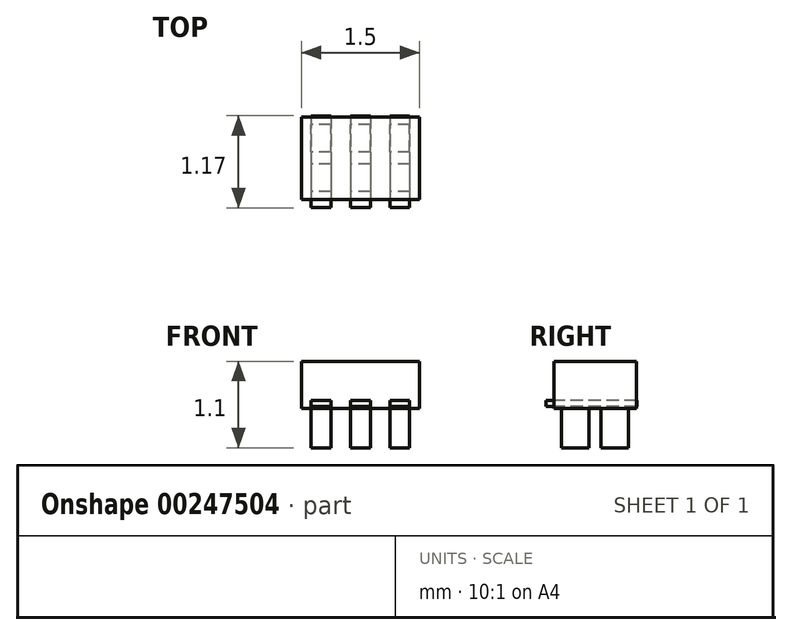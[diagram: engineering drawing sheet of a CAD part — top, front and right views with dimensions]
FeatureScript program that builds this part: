
annotation { "Feature Type Name" : "Feature", "Feature Type Description" : "" }
export const myFeature = defineFeature(function(context is Context, id is Id, definition is map)
    precondition{}
    {
        {
            var Q0;
            Q0=qCreatedBy(makeId("Top.planeOp"),FACE);
            var sketch = newSketch(context, id + "F0", { "sketchPlane" : qUnion([Q0])});
            skLineSegment(sketch, "E0.bottom", {"start": v(0.75, -0.53) * mm, "end": v(-0.75, -0.53) * mm});
            skLineSegment(sketch, "E0.top", {"start": v(0.75, 0.53) * mm, "end": v(-0.75, 0.53) * mm});
            skLineSegment(sketch, "E0.left", {"start": v(0.75, -0.53) * mm, "end": v(0.75, 0.53) * mm});
            skLineSegment(sketch, "E0.right", {"start": v(-0.75, -0.53) * mm, "end": v(-0.75, 0.52) * mm});
            skPoint(sketch, "E0.middle", {"position": v(0, 0) * mm});
            skSolve(sketch);
        }
        {
            var Q0;
            Q0=qSketchRegion(id+"F0",true);
            extrude(context, id + "F1", {"entities" : qUnion([Q0]), "depth" : .6 * mm});
        }
        {
            var Q0;
            Q0=makeQuery(id+"F1.opExtrude","CAP_FACE",FACE,{"disambiguationData":[OSD([sQuery(id+"F0.wireOp",EDGE,"E0.bottom"),sQuery(id+"F0.wireOp",EDGE,"E0.top"),sQuery(id+"F0.wireOp",EDGE,"E0.left"),sQuery(id+"F0.wireOp",EDGE,"E0.right")])],"isStart":true});
            var sketch = newSketch(context, id + "F2", { "sketchPlane" : qUnion([Q0])});
            skLineSegment(sketch, "E1", {"start": v(0, 0.53) * mm, "end": v(0, -0.53) * mm, "construction": true});
            skLineSegment(sketch, "E2", {"start": v(-0.75, 0) * mm, "end": v(0.75, 0) * mm, "construction": true});
            skLineSegment(sketch, "E3.bottom", {"start": v(-0.37, 0.08) * mm, "end": v(-0.62, 0.08) * mm});
            skLineSegment(sketch, "E3.top", {"start": v(-0.38, 0.43) * mm, "end": v(-0.63, 0.43) * mm});
            skLineSegment(sketch, "E3.left", {"start": v(-0.37, 0.08) * mm, "end": v(-0.38, 0.43) * mm});
            skLineSegment(sketch, "E3.right", {"start": v(-0.62, 0.08) * mm, "end": v(-0.63, 0.43) * mm});
            skPoint(sketch, "E3.middle", {"position": v(-0.5, 0.25) * mm});
            skLineSegment(sketch, "E4.1.0.0", {"start": v(0.13, 0.08) * mm, "end": v(0.12, 0.43) * mm});
            skLineSegment(sketch, "E4.1.0.1", {"start": v(0.12, 0.43) * mm, "end": v(-0.13, 0.43) * mm});
            skLineSegment(sketch, "E4.1.0.2", {"start": v(-0.12, 0.08) * mm, "end": v(-0.13, 0.43) * mm});
            skLineSegment(sketch, "E4.1.0.3", {"start": v(0.13, 0.08) * mm, "end": v(-0.12, 0.08) * mm});
            skLineSegment(sketch, "E4.2.0.0", {"start": v(0.62, 0.08) * mm, "end": v(0.62, 0.43) * mm});
            skLineSegment(sketch, "E4.2.0.1", {"start": v(0.62, 0.43) * mm, "end": v(0.37, 0.43) * mm});
            skLineSegment(sketch, "E4.2.0.2", {"start": v(0.38, 0.08) * mm, "end": v(0.37, 0.43) * mm});
            skLineSegment(sketch, "E4.2.0.3", {"start": v(0.63, 0.08) * mm, "end": v(0.38, 0.08) * mm});
            skLineSegment(sketch, "E4.direction1", {"start": v(-0.37, 0.08) * mm, "end": v(0.13, 0.08) * mm, "construction": true});
            skLineSegment(sketch, "E5.MirrorCS", {"start": v(0.13, -0.08) * mm, "end": v(-0.12, -0.08) * mm});
            skLineSegment(sketch, "E6.MirrorCS", {"start": v(0.12, -0.08) * mm, "end": v(0.12, -0.43) * mm});
            skLineSegment(sketch, "E7.MirrorCS", {"start": v(-0.62, -0.07) * mm, "end": v(-0.63, -0.42) * mm});
            skLineSegment(sketch, "E8.MirrorCS", {"start": v(-0.38, -0.07) * mm, "end": v(-0.38, -0.42) * mm});
            skLineSegment(sketch, "E9.MirrorCS", {"start": v(-0.38, -0.43) * mm, "end": v(-0.63, -0.42) * mm});
            skLineSegment(sketch, "E10.MirrorCS", {"start": v(-0.37, -0.07) * mm, "end": v(-0.62, -0.07) * mm});
            skLineSegment(sketch, "E11.MirrorCS", {"start": v(-0.38, -0.07) * mm, "end": v(0.13, -0.08) * mm, "construction": true});
            skLineSegment(sketch, "E12.MirrorCS", {"start": v(0.63, -0.08) * mm, "end": v(0.38, -0.08) * mm});
            skPoint(sketch, "E13.MirrorP", {"position": v(-0.5, -0.25) * mm});
            skLineSegment(sketch, "E14.MirrorCS", {"start": v(0.12, -0.43) * mm, "end": v(-0.13, -0.43) * mm});
            skLineSegment(sketch, "E15.MirrorCS", {"start": v(-0.12, -0.08) * mm, "end": v(-0.13, -0.43) * mm});
            skLineSegment(sketch, "E16.MirrorCS", {"start": v(0.62, -0.08) * mm, "end": v(0.62, -0.43) * mm});
            skLineSegment(sketch, "E17.MirrorCS", {"start": v(0.62, -0.43) * mm, "end": v(0.37, -0.43) * mm});
            skLineSegment(sketch, "E18.MirrorCS", {"start": v(0.38, -0.08) * mm, "end": v(0.37, -0.43) * mm});
            skSolve(sketch);
        }
        {
            var Q0;
            Q0=qSketchRegion(id+"F2",true);
            extrude(context, id + "F3", {"entities" : qUnion([Q0]), "operationType" : NewBodyOperationType.ADD, "depth" : .5 * mm});
        }
        {
            var Q0;
            Q0=makeQuery(id+"F1.opExtrude","SWEPT_FACE",FACE,{"disambiguationData":[OSD([sQuery(id+"F0.wireOp",EDGE,"E0.bottom")])]});
            var sketch = newSketch(context, id + "F4", { "sketchPlane" : qUnion([Q0])});
            skLineSegment(sketch, "E19", {"start": v(0, 0) * mm, "end": v(0, 0.6) * mm, "construction": true});
            skLineSegment(sketch, "E20.bottom", {"start": v(-0.38, 0.03) * mm, "end": v(-0.63, 0.03) * mm});
            skLineSegment(sketch, "E20.top", {"start": v(-0.38, 0.1) * mm, "end": v(-0.63, 0.1) * mm});
            skLineSegment(sketch, "E20.left", {"start": v(-0.38, 0.03) * mm, "end": v(-0.38, 0.1) * mm});
            skLineSegment(sketch, "E20.right", {"start": v(-0.63, 0.03) * mm, "end": v(-0.63, 0.1) * mm});
            skPoint(sketch, "E20.middle", {"position": v(-0.5, 0.06) * mm});
            skLineSegment(sketch, "E21.1.0.0", {"start": v(0.12, 0.03) * mm, "end": v(-0.13, 0.03) * mm});
            skLineSegment(sketch, "E21.1.0.1", {"start": v(0.12, 0.1) * mm, "end": v(-0.13, 0.1) * mm});
            skLineSegment(sketch, "E21.1.0.2", {"start": v(0.12, 0.03) * mm, "end": v(0.12, 0.1) * mm});
            skLineSegment(sketch, "E21.1.0.3", {"start": v(-0.13, 0.03) * mm, "end": v(-0.13, 0.1) * mm});
            skPoint(sketch, "E21.1.0.4", {"position": v(0, 0.06) * mm});
            skLineSegment(sketch, "E21.2.0.0", {"start": v(0.62, 0.03) * mm, "end": v(0.37, 0.03) * mm});
            skLineSegment(sketch, "E21.2.0.1", {"start": v(0.62, 0.1) * mm, "end": v(0.37, 0.1) * mm});
            skLineSegment(sketch, "E21.2.0.2", {"start": v(0.62, 0.03) * mm, "end": v(0.62, 0.1) * mm});
            skLineSegment(sketch, "E21.2.0.3", {"start": v(0.37, 0.03) * mm, "end": v(0.37, 0.1) * mm});
            skPoint(sketch, "E21.2.0.4", {"position": v(0.5, 0.06) * mm});
            skLineSegment(sketch, "E21.direction1", {"start": v(-0.63, 0.03) * mm, "end": v(-0.13, 0.03) * mm, "construction": true});
            skSolve(sketch);
        }
        {
            var Q0;
            Q0=qSketchRegion(id+"F4",true);
            extrude(context, id + "F5", {"entities" : qUnion([Q0]), "oppositeDirection" : true, "depth" : 1.06 * mm, "hasSecondDirection" : true, "secondDirectionOppositeDirection" : false, "secondDirectionDepth" : .1 * mm});
        }
    });
